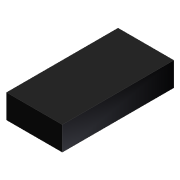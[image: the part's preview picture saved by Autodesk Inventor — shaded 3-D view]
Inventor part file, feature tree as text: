
AUTODESK INVENTOR PART (.ipt)
format: ipt  version: unknown  size: 166,912 bytes
history: native  units: mm
features: extrude x1, sketch x1
ambient origin geometry x8: Origin, YZ Plane, XZ Plane, XY Plane, X Axis, Y Axis, Z Axis, Center Point
feature tree (2):
  extrude  "Выдавливание2"  Depth=3.5mm
  sketch  "Эскиз2"
